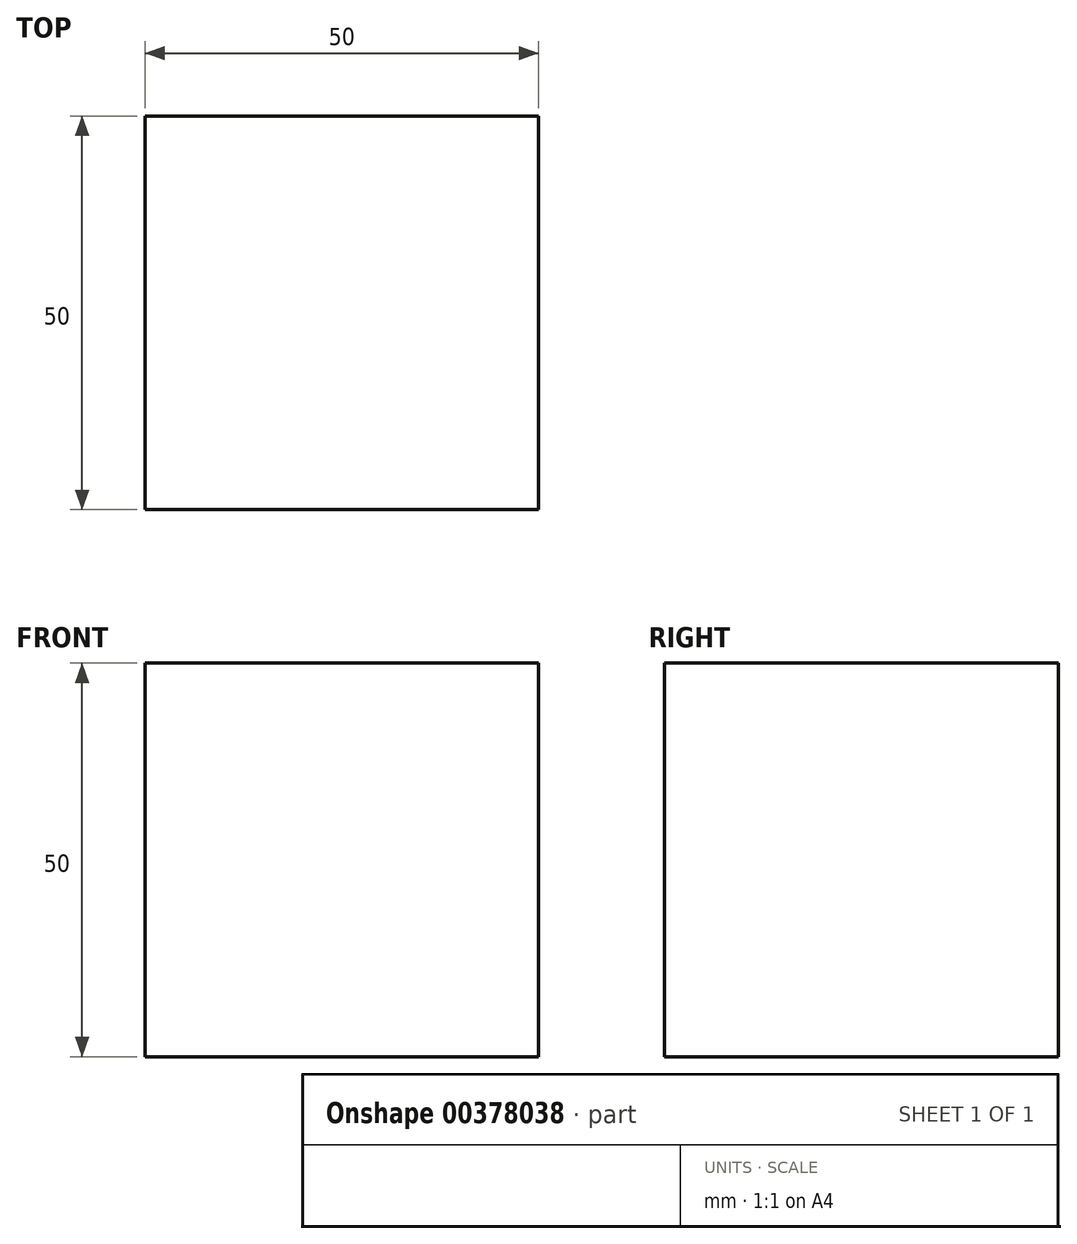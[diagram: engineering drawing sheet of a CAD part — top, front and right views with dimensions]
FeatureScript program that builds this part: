
annotation { "Feature Type Name" : "Feature", "Feature Type Description" : "" }
export const myFeature = defineFeature(function(context is Context, id is Id, definition is map)
    precondition{}
    {
        {
            var Q0;
            Q0=qCreatedBy(makeId("Front.planeOp"),FACE);
            var sketch = newSketch(context, id + "F0", { "sketchPlane" : qUnion([Q0])});
            skLineSegment(sketch, "E0.bottom", {"start": v(0, 0.75) * mm, "end": v(50, 0.75) * mm});
            skLineSegment(sketch, "E0.top", {"start": v(0, 50.75) * mm, "end": v(50, 50.75) * mm});
            skLineSegment(sketch, "E0.left", {"start": v(0, 0.75) * mm, "end": v(0, 50.75) * mm});
            skLineSegment(sketch, "E0.right", {"start": v(50, 0.75) * mm, "end": v(50, 50.75) * mm});
            skSolve(sketch);
        }
        {
            var Q0;
            Q0=makeQuery(id+"F0.imprint","IMPRINT",FACE,{"disambiguationData":[TD([[makeQuery(id+"F0.imprint","IMPRINT",EDGE,{"derivedFrom":sQuery(id+"F0.wireOp",EDGE,"E0.bottom")}),1.0]])]});
            extrude(context, id + "F1", {"entities" : qUnion([Q0]), "oppositeDirection" : true, "depth" : 50 * mm});
        }
    });
